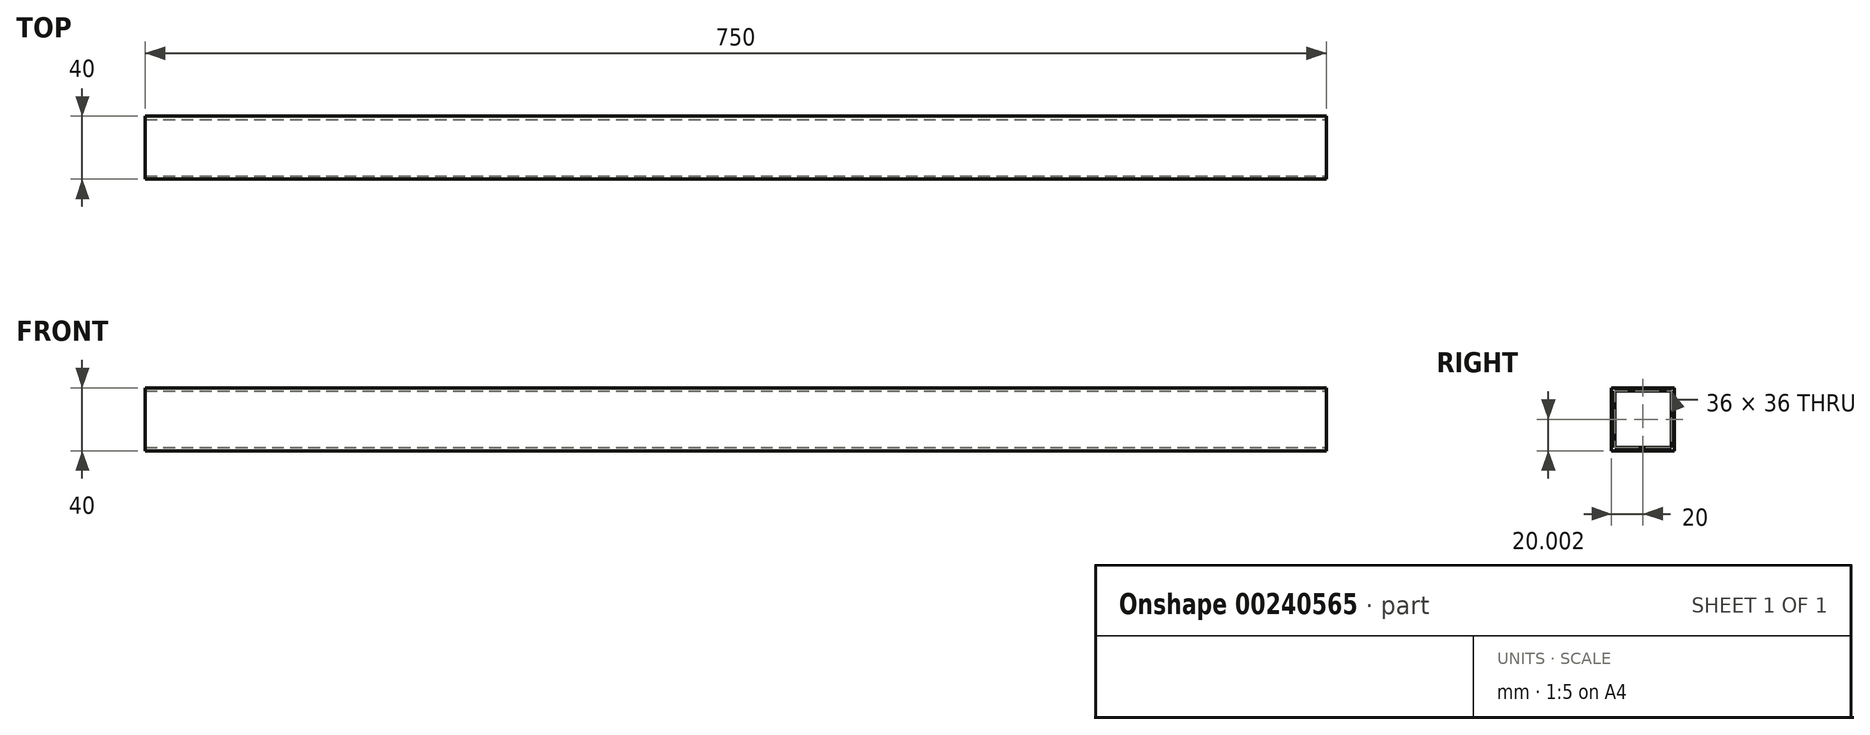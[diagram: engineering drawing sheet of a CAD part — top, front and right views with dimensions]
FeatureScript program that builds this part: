
annotation { "Feature Type Name" : "Feature", "Feature Type Description" : "" }
export const myFeature = defineFeature(function(context is Context, id is Id, definition is map)
    precondition{}
    {
        {
            var Q0;
            Q0=qCreatedBy(makeId("Front.planeOp"),FACE);
            var sketch = newSketch(context, id + "F0", { "sketchPlane" : qUnion([Q0])});
            skLineSegment(sketch, "E0.bottom", {"start": v(-676.08, 35.76) * mm, "end": v(73.92, 35.76) * mm});
            skLineSegment(sketch, "E0.top", {"start": v(-676.08, -4.24) * mm, "end": v(73.92, -4.24) * mm});
            skLineSegment(sketch, "E0.left", {"start": v(-676.08, 35.76) * mm, "end": v(-676.08, -4.24) * mm});
            skLineSegment(sketch, "E0.right", {"start": v(73.92, 35.76) * mm, "end": v(73.92, -4.24) * mm});
            skSolve(sketch);
        }
        {
            var Q0;
            Q0=makeQuery(id+"F0.imprint","IMPRINT",FACE,{"disambiguationData":[TD([[makeQuery(id+"F0.imprint","IMPRINT",EDGE,{"derivedFrom":sQuery(id+"F0.wireOp",EDGE,"E0.bottom")}),-1.0]])]});
            extrude(context, id + "F1", {"entities" : qUnion([Q0]), "depth" : 40 * mm});
        }
        {
            var Q0;
            Q0=makeQuery(id+"F1.opExtrude","SWEPT_FACE",FACE,{"disambiguationData":[OSD([sQuery(id+"F0.wireOp",EDGE,"E0.left")])]});
            var Q1;
            Q1=makeQuery(id+"F1.opExtrude","SWEPT_FACE",FACE,{"disambiguationData":[OSD([sQuery(id+"F0.wireOp",EDGE,"E0.right")])]});
            shell(context, id + "F2", {"entities" : qUnion([Q0, Q1]), "thickness" : 2 * mm});
        }
    });
